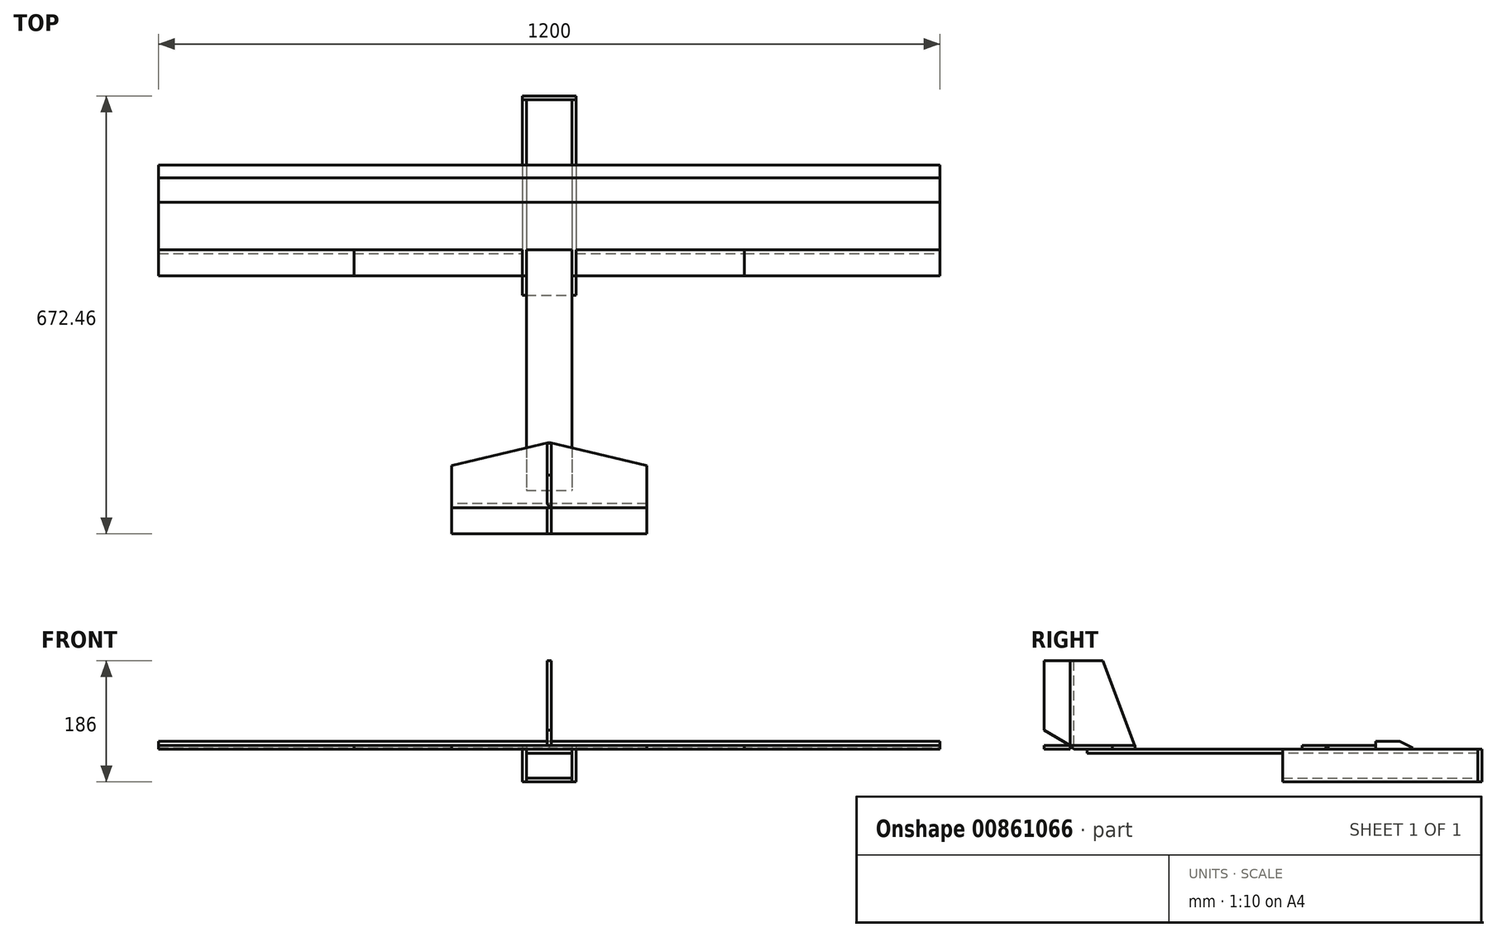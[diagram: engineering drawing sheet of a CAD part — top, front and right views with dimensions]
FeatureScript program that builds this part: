
annotation { "Feature Type Name" : "Feature", "Feature Type Description" : "" }
export const myFeature = defineFeature(function(context is Context, id is Id, definition is map)
    precondition{}
    {
        {
            var Q0;
            Q0=qCreatedBy(makeId("Top.planeOp"),FACE);
            var sketch = newSketch(context, id + "F0", { "sketchPlane" : qUnion([Q0])});
            skLineSegment(sketch, "E0.bottom", {"start": v(-35, 150) * mm, "end": v(35, 150) * mm});
            skLineSegment(sketch, "E0.top", {"start": v(-35, -150) * mm, "end": v(35, -150) * mm});
            skLineSegment(sketch, "E0.left", {"start": v(-35, 150) * mm, "end": v(-35, -150) * mm});
            skLineSegment(sketch, "E0.right", {"start": v(35, 150) * mm, "end": v(35, -150) * mm});
            skPoint(sketch, "E0.middle", {"position": v(0, 0) * mm});
            skLineSegment(sketch, "E1.top", {"start": v(-35, -450) * mm, "end": v(35, -450) * mm});
            skLineSegment(sketch, "E1.left", {"start": v(-35, -150) * mm, "end": v(-35, -450) * mm});
            skLineSegment(sketch, "E1.right", {"start": v(35, -150) * mm, "end": v(35, -450) * mm});
            skLineSegment(sketch, "E2.bottom", {"start": v(35, 150) * mm, "end": v(41, 150) * mm});
            skLineSegment(sketch, "E2.top", {"start": v(35, -150) * mm, "end": v(41, -150) * mm});
            skLineSegment(sketch, "E2.right", {"start": v(41, 150) * mm, "end": v(41, -150) * mm});
            skLineSegment(sketch, "E3.bottom", {"start": v(-35, 150) * mm, "end": v(-41, 150) * mm});
            skLineSegment(sketch, "E3.top", {"start": v(-35, -150) * mm, "end": v(-41, -150) * mm});
            skLineSegment(sketch, "E3.right", {"start": v(-41, 150) * mm, "end": v(-41, -150) * mm});
            skLineSegment(sketch, "E4.bottom", {"start": v(-41, -150) * mm, "end": v(-35, -150) * mm});
            skLineSegment(sketch, "E4.top", {"start": v(-41, -450) * mm, "end": v(-35, -450) * mm});
            skLineSegment(sketch, "E4.left", {"start": v(-41, -150) * mm, "end": v(-41, -450) * mm});
            skLineSegment(sketch, "E5.bottom", {"start": v(41, -150) * mm, "end": v(35, -150) * mm});
            skLineSegment(sketch, "E5.top", {"start": v(41, -450) * mm, "end": v(35, -450) * mm});
            skLineSegment(sketch, "E5.left", {"start": v(41, -150) * mm, "end": v(41, -450) * mm});
            skSolve(sketch);
        }
        {
            var Q0;
            Q0=makeQuery(id+"F0.imprint","IMPRINT",FACE,{"disambiguationData":[TD([[makeQuery(id+"F0.imprint","IMPRINT",EDGE,{"derivedFrom":sQuery(id+"F0.wireOp",EDGE,"E0.bottom")}),-1.0]])]});
            var Q1;
            Q1=makeQuery(id+"F0.imprint","IMPRINT",FACE,{"disambiguationData":[TD([[makeQuery(id+"F0.imprint","IMPRINT",EDGE,{"derivedFrom":sQuery(id+"F0.wireOp",EDGE,"E0.top")}),-1.0]])]});
            extrude(context, id + "F1", {"entities" : qUnion([Q0, Q1]), "oppositeDirection" : true, "depth" : 6 * mm, "offsetDistance" : 25 * mm});
        }
        {
            var Q0;
            Q0=makeQuery(id+"F0.imprint","IMPRINT",FACE,{"disambiguationData":[TD([[makeQuery(id+"F0.imprint","IMPRINT",EDGE,{"derivedFrom":sQuery(id+"F0.wireOp",EDGE,"E3.bottom")}),1.0]])]});
            var Q1;
            Q1=makeQuery(id+"F0.imprint","IMPRINT",FACE,{"disambiguationData":[TD([[makeQuery(id+"F0.imprint","IMPRINT",EDGE,{"derivedFrom":sQuery(id+"F0.wireOp",EDGE,"E2.bottom")}),-1.0]])]});
            var Q2;
            Q2=makeQuery(id+"F0.imprint","IMPRINT",FACE,{"disambiguationData":[TD([[makeQuery(id+"F0.imprint","IMPRINT",EDGE,{"derivedFrom":sQuery(id+"F0.wireOp",EDGE,"E5.bottom")}),1.0]])]});
            var Q3;
            Q3=makeQuery(id+"F0.imprint","IMPRINT",FACE,{"disambiguationData":[TD([[makeQuery(id+"F0.imprint","IMPRINT",EDGE,{"derivedFrom":sQuery(id+"F0.wireOp",EDGE,"E4.bottom")}),-1.0]])]});
            extrude(context, id + "F2", {"entities" : qUnion([Q0, Q1, Q2, Q3]), "oppositeDirection" : true, "depth" : 50 * mm, "offsetDistance" : 25 * mm});
        }
        {
            var Q0;
            Q0=makeQuery(id+"F2.opExtrude","SWEPT_FACE",FACE,{"disambiguationData":[OSD([sQuery(id+"F0.wireOp",EDGE,"E2.right"),sQuery(id+"F0.wireOp",EDGE,"E5.left")])]});
            var sketch = newSketch(context, id + "F3", { "sketchPlane" : qUnion([Q0])});
            skLineSegment(sketch, "E6", {"start": v(-150, 0) * mm, "end": v(-150, -50) * mm, "construction": true});
            skLineSegment(sketch, "E7", {"start": v(-150, -50) * mm, "end": v(-450, -15) * mm});
            skLineSegment(sketch, "E8", {"start": v(-450, -15) * mm, "end": v(-450, 0) * mm, "construction": true});
            skLineSegment(sketch, "E9", {"start": v(-450, 0) * mm, "end": v(-150, 0) * mm, "construction": true});
            skLineSegment(sketch, "E10", {"start": v(-450, -15) * mm, "end": v(-450, -50) * mm});
            skLineSegment(sketch, "E11", {"start": v(-450, -50) * mm, "end": v(-150, -50) * mm});
            skSolve(sketch);
        }
        {
            var Q0;
            Q0=makeQuery(id+"F2.opExtrude","SWEPT_FACE",FACE,{"disambiguationData":[OSD([sQuery(id+"F0.wireOp",EDGE,"E3.right"),sQuery(id+"F0.wireOp",EDGE,"E4.left")])]});
            var sketch = newSketch(context, id + "F4", { "sketchPlane" : qUnion([Q0])});
            skLineSegment(sketch, "E12", {"start": v(150, 0) * mm, "end": v(150, -50) * mm, "construction": true});
            skLineSegment(sketch, "E13", {"start": v(150, 0) * mm, "end": v(450, 0) * mm, "construction": true});
            skLineSegment(sketch, "E14", {"start": v(450, 0) * mm, "end": v(450, -15) * mm, "construction": true});
            skLineSegment(sketch, "E15", {"start": v(450, -15) * mm, "end": v(150, -50) * mm});
            skLineSegment(sketch, "E16", {"start": v(450, -50) * mm, "end": v(150, -50) * mm});
            skLineSegment(sketch, "E17", {"start": v(450, -15) * mm, "end": v(450, -50) * mm});
            skSolve(sketch);
        }
        {
            var Q0;
            Q0 = qSketchRegion(id + "F4", true);
            var Q1;
            Q1 = qSketchRegion(id + "F3", true);
            extrude(context, id + "F5", {"entities" : qUnion([Q0, Q1]), "operationType" : NewBodyOperationType.REMOVE, "endBound" : BoundingType.THROUGH_ALL, "depth" : 6 * mm, "offsetDistance" : 25 * mm});
        }
        {
            var Q0;
            Q0=makeQuery(id+"F2.opExtrude","SWEPT_FACE",FACE,{"disambiguationData":[OSD([sQuery(id+"F0.wireOp",EDGE,"E0.right"),sQuery(id+"F0.wireOp",EDGE,"E1.right")])]});
            var sketch = newSketch(context, id + "F6", { "sketchPlane" : qUnion([Q0])});
            skLineSegment(sketch, "E18.bottom", {"start": v(150, -50) * mm, "end": v(-150, -50) * mm});
            skLineSegment(sketch, "E18.top", {"start": v(150, -44) * mm, "end": v(-150, -44) * mm});
            skLineSegment(sketch, "E18.left", {"start": v(-150, -50) * mm, "end": v(-150, -44) * mm});
            skLineSegment(sketch, "E18.right", {"start": v(150, -50) * mm, "end": v(150, -44) * mm});
            skLineSegment(sketch, "E19", {"start": v(450, -15) * mm, "end": v(449.3, -9.04) * mm});
            skLineSegment(sketch, "E20", {"start": v(449.3, -9.04) * mm, "end": v(150, -44) * mm});
            skSolve(sketch);
        }
        {
            var Q0;
            Q0=makeQuery(id+"F6.imprint","IMPRINT",FACE,{"disambiguationData":[TD([[makeQuery(id+"F6.imprint","IMPRINT",EDGE,{"derivedFrom":sQuery(id+"F6.wireOp",EDGE,"E18.bottom")}),1.0]])]});
            var Q1;
            Q1=makeQuery(id+"F6.imprint","IMPRINT",FACE,{"disambiguationData":[TD([[makeQuery(id+"F6.imprint","IMPRINT",EDGE,{"derivedFrom":sQuery(id+"F6.wireOp",EDGE,"E18.right")}),-1.0]])]});
            extrude(context, id + "F7", {"entities" : qUnion([Q0, Q1]), "depth" : 70 * mm, "offsetDistance" : 25 * mm});
        }
        {
            var Q0;
            Q0=makeQuery(id+"F2.opExtrude","SWEPT_FACE",FACE,{"disambiguationData":[OSD([sQuery(id+"F0.wireOp",EDGE,"E2.bottom")])]});
            var sketch = newSketch(context, id + "F8", { "sketchPlane" : qUnion([Q0])});
            skLineSegment(sketch, "E21.bottom", {"start": v(-41, 0) * mm, "end": v(41, 0) * mm});
            skLineSegment(sketch, "E21.top", {"start": v(-41, -50) * mm, "end": v(41, -50) * mm});
            skLineSegment(sketch, "E21.left", {"start": v(-41, 0) * mm, "end": v(-41, -50) * mm});
            skLineSegment(sketch, "E21.right", {"start": v(41, 0) * mm, "end": v(41, -50) * mm});
            skPoint(sketch, "E21.middle", {"position": v(0, -25) * mm});
            skPoint(sketch, "E22.start.orphan", {"position": v(-35, -25) * mm});
            skSolve(sketch);
        }
        {
            var Q0;
            Q0 = qSketchRegion(id + "F8", true);
            extrude(context, id + "F9", {"entities" : qUnion([Q0]), "depth" : 6 * mm, "offsetDistance" : 25 * mm});
        }
        {
            var Q0;
            Q0=makeQuery(id+"F1.opExtrude","CAP_FACE",FACE,{"disambiguationData":[OSD([sQuery(id+"F0.wireOp",EDGE,"E0.bottom"),sQuery(id+"F0.wireOp",EDGE,"E1.top"),sQuery(id+"F0.wireOp",EDGE,"E0.right"),sQuery(id+"F0.wireOp",EDGE,"E0.left"),sQuery(id+"F0.wireOp",EDGE,"E1.left"),sQuery(id+"F0.wireOp",EDGE,"E1.right")])],"isStart":true});
            var sketch = newSketch(context, id + "F10", { "sketchPlane" : qUnion([Q0])});
            skLineSegment(sketch, "E23.bottom", {"start": v(150, -476.37) * mm, "end": v(-150, -476.37) * mm});
            skLineSegment(sketch, "E23.top", {"start": v(150, -376.37) * mm, "end": v(-150, -376.37) * mm});
            skLineSegment(sketch, "E23.left", {"start": v(150, -426.37) * mm, "end": v(150, -376.37) * mm});
            skLineSegment(sketch, "E23.right", {"start": v(-150, -426.37) * mm, "end": v(-150, -376.37) * mm});
            skPoint(sketch, "E23.middle", {"position": v(0, -426.37) * mm});
            skPoint(sketch, "E24", {"position": v(0, -450) * mm});
            skLineSegment(sketch, "E25", {"start": v(0, -426.37) * mm, "end": v(0, -376.37) * mm});
            skLineSegment(sketch, "E26", {"start": v(0, -426.37) * mm, "end": v(-150, -426.37) * mm, "construction": true});
            skLineSegment(sketch, "E27", {"start": v(0, -426.37) * mm, "end": v(150, -426.37) * mm, "construction": true});
            skLineSegment(sketch, "E28", {"start": v(0, -376.37) * mm, "end": v(-150, -411.37) * mm});
            skLineSegment(sketch, "E29", {"start": v(0, -376.37) * mm, "end": v(150, -411.37) * mm});
            skLineSegment(sketch, "E30", {"start": v(-150, -426.37) * mm, "end": v(-150, -476.37) * mm});
            skLineSegment(sketch, "E31", {"start": v(150, -476.37) * mm, "end": v(150, -426.37) * mm});
            skSolve(sketch);
        }
        {
            var Q0;
            Q0=makeQuery(id+"F10.imprint","IMPRINT",FACE,{"disambiguationData":[TD([[makeQuery(id+"F10.imprint","IMPRINT",EDGE,{"derivedFrom":sQuery(id+"F10.wireOp",EDGE,"E23.bottom")}),-1.0]])]});
            var Q1;
            {var subQ1=makeQuery(id+"F1.opExtrude","CAP_EDGE",EDGE,{"disambiguationData":[OSD([sQuery(id+"F0.wireOp",EDGE,"E1.top")])],"isStart":true});Q1=makeQuery(id+"F10.imprint","IMPRINT",FACE,{"disambiguationData":[TD([[makeQuery(id+"F10.imprint","IMPRINT",EDGE,{"derivedFrom":subQ1}),1.0]])]});}
            extrude(context, id + "F11", {"entities" : qUnion([Q0, Q1]), "depth" : 6 * mm, "offsetDistance" : 25 * mm});
        }
        {
            var Q0;
            Q0=makeQuery(id+"F1.opExtrude","CAP_FACE",FACE,{"disambiguationData":[OSD([sQuery(id+"F0.wireOp",EDGE,"E0.bottom"),sQuery(id+"F0.wireOp",EDGE,"E1.top"),sQuery(id+"F0.wireOp",EDGE,"E0.right"),sQuery(id+"F0.wireOp",EDGE,"E0.left"),sQuery(id+"F0.wireOp",EDGE,"E1.left"),sQuery(id+"F0.wireOp",EDGE,"E1.right")])],"isStart":true});
            var sketch = newSketch(context, id + "F12", { "sketchPlane" : qUnion([Q0])});
            skLineSegment(sketch, "E32", {"start": v(0, 60) * mm, "end": v(0, -90) * mm, "construction": true});
            skLineSegment(sketch, "E33.bottom", {"start": v(-600, 50) * mm, "end": v(600, 50) * mm});
            skLineSegment(sketch, "E33.top", {"start": v(-600, -80) * mm, "end": v(600, -80) * mm});
            skLineSegment(sketch, "E33.left", {"start": v(-600, 50) * mm, "end": v(-600, -80) * mm});
            skLineSegment(sketch, "E33.right", {"start": v(600, 50) * mm, "end": v(600, -80) * mm});
            skPoint(sketch, "E33.middle", {"position": v(0, -15) * mm});
            skLineSegment(sketch, "E34", {"start": v(-600, -7.2) * mm, "end": v(600, -7.2) * mm});
            skLineSegment(sketch, "E35.bottom", {"start": v(-41, -80) * mm, "end": v(41, -80) * mm});
            skLineSegment(sketch, "E35.top", {"start": v(-41, -120) * mm, "end": v(41, -120) * mm});
            skLineSegment(sketch, "E35.left", {"start": v(-41, -80) * mm, "end": v(-41, -120) * mm});
            skLineSegment(sketch, "E35.right", {"start": v(41, -80) * mm, "end": v(41, -120) * mm});
            skSolve(sketch);
        }
        {
            var Q0;
            {var subQ0=sQuery(id+"F12.wireOp",EDGE,"E33.left");var subQ1=sQuery(id+"F12.wireOp",EDGE,"E33.top");var subQ2=makeQuery(id+"F12.imprint","INTERSECT",VERTEX,{"derivedFrom":[subQ1,subQ0]});Q0=makeQuery(id+"F12.imprint","IMPRINT",FACE,{"disambiguationData":[TD([[makeQuery(id+"F12.imprint","IMPRINT",EDGE,{"disambiguationData":[TD([[subQ2,1.0]])],"derivedFrom":subQ0}),1.0]])]});}
            var Q1;
            {var subQ0=sQuery(id+"F12.wireOp",EDGE,"E33.right");var subQ1=sQuery(id+"F12.wireOp",EDGE,"E33.top");var subQ2=makeQuery(id+"F12.imprint","INTERSECT",VERTEX,{"derivedFrom":[subQ1,subQ0]});Q1=makeQuery(id+"F12.imprint","IMPRINT",FACE,{"disambiguationData":[TD([[makeQuery(id+"F12.imprint","IMPRINT",EDGE,{"disambiguationData":[TD([[subQ2,1.0]])],"derivedFrom":subQ0}),-1.0]])]});}
            var Q2;
            {var subQ0=sQuery(id+"F12.wireOp",EDGE,"E33.top");var subQ1=makeQuery(id+"F1.opExtrude","CAP_EDGE",EDGE,{"disambiguationData":[OSD([sQuery(id+"F0.wireOp",EDGE,"E0.left"),sQuery(id+"F0.wireOp",EDGE,"E1.left")])],"isStart":true});var subQ2=makeQuery(id+"F12.imprint","INTERSECT",VERTEX,{"derivedFrom":[subQ1,subQ0]});Q2=makeQuery(id+"F12.imprint","IMPRINT",FACE,{"disambiguationData":[TD([[makeQuery(id+"F12.imprint","IMPRINT",EDGE,{"disambiguationData":[TD([[subQ2,-1.0]])],"derivedFrom":subQ0}),1.0]])]});}
            var Q3;
            {var subQ0=sQuery(id+"F12.wireOp",EDGE,"E34");var subQ1=makeQuery(id+"F1.opExtrude","CAP_EDGE",EDGE,{"disambiguationData":[OSD([sQuery(id+"F0.wireOp",EDGE,"E0.left"),sQuery(id+"F0.wireOp",EDGE,"E1.left")])],"isStart":true});var subQ2=makeQuery(id+"F12.imprint","INTERSECT",VERTEX,{"derivedFrom":[subQ1,subQ0]});Q3=makeQuery(id+"F12.imprint","IMPRINT",FACE,{"disambiguationData":[TD([[makeQuery(id+"F12.imprint","IMPRINT",EDGE,{"disambiguationData":[TD([[subQ2,-1.0]])],"derivedFrom":subQ0}),-1.0]])]});}
            var Q4;
            {var subQ0=sQuery(id+"F12.wireOp",EDGE,"E35.bottom");var subQ1=makeQuery(id+"F1.opExtrude","CAP_EDGE",EDGE,{"disambiguationData":[OSD([sQuery(id+"F0.wireOp",EDGE,"E0.left"),sQuery(id+"F0.wireOp",EDGE,"E1.left")])],"isStart":true});var subQ2=makeQuery(id+"F12.imprint","INTERSECT",VERTEX,{"derivedFrom":[subQ1,subQ0]});Q4=makeQuery(id+"F12.imprint","IMPRINT",FACE,{"disambiguationData":[TD([[makeQuery(id+"F12.imprint","IMPRINT",EDGE,{"disambiguationData":[TD([[subQ2,-1.0]])],"derivedFrom":subQ0}),-1.0]])]});}
            var Q5;
            {var subQ0=sQuery(id+"F12.wireOp",EDGE,"E35.right");Q5=makeQuery(id+"F12.imprint","IMPRINT",FACE,{"disambiguationData":[TD([[makeQuery(id+"F12.imprint","IMPRINT",EDGE,{"derivedFrom":subQ0}),-1.0]])]});}
            var Q6;
            {var subQ0=sQuery(id+"F12.wireOp",EDGE,"E35.left");Q6=makeQuery(id+"F12.imprint","IMPRINT",FACE,{"disambiguationData":[TD([[makeQuery(id+"F12.imprint","IMPRINT",EDGE,{"derivedFrom":subQ0}),1.0]])]});}
            extrude(context, id + "F13", {"entities" : qUnion([Q0, Q1, Q2, Q3, Q4, Q5, Q6]), "depth" : 6 * mm, "offsetDistance" : 25 * mm});
        }
        {
            var Q0;
            {var subQ0=sQuery(id+"F12.wireOp",EDGE,"f9qtTOJY-V2A6-egXc-k2BP-GJsxi0lqYclH");var subQ1=sQuery(id+"F12.wireOp",EDGE,"LZZIuyLF-FcuM-KAbS-gqD7-LItA6hUNZmsj");var subQ2=makeQuery(id+"F12.imprint","INTERSECT",VERTEX,{"derivedFrom":[subQ1,subQ0]});Q0=makeQuery(id+"F12.imprint","IMPRINT",FACE,{"disambiguationData":[TD([[makeQuery(id+"F12.imprint","IMPRINT",EDGE,{"disambiguationData":[TD([[subQ2,-1.0]])],"derivedFrom":subQ0}),1.0]])]});}
            var Q1;
            {var subQ5=sQuery(id+"F12.wireOp",EDGE,"1fCqvdx0-kBV5-oBVe-sgTc-qIVpe4zWd1In");var subQ7=sQuery(id+"F12.wireOp",EDGE,"LZZIuyLF-FcuM-KAbS-gqD7-LItA6hUNZmsj");var subQ8=makeQuery(id+"F12.imprint","INTERSECT",VERTEX,{"derivedFrom":[subQ7,subQ5]});Q1=makeQuery(id+"F12.imprint","IMPRINT",FACE,{"disambiguationData":[TD([[makeQuery(id+"F12.imprint","IMPRINT",EDGE,{"disambiguationData":[TD([[subQ8,-1.0]])],"derivedFrom":subQ7}),1.0]])]});}
            var Q2;
            {var subQ0=sQuery(id+"F12.wireOp",EDGE,"7Yiizx21-BXyQ-pYym-OMHb-G3uuBtVVquUZ");var subQ1=sQuery(id+"F12.wireOp",EDGE,"1fCqvdx0-kBV5-oBVe-sgTc-qIVpe4zWd1In");var subQ2=makeQuery(id+"F12.imprint","INTERSECT",VERTEX,{"derivedFrom":[subQ1,subQ0]});Q2=makeQuery(id+"F12.imprint","IMPRINT",FACE,{"disambiguationData":[TD([[makeQuery(id+"F12.imprint","IMPRINT",EDGE,{"disambiguationData":[TD([[subQ2,-1.0]])],"derivedFrom":subQ0}),-1.0]])]});}
            var Q3;
            {var subQ0=sQuery(id+"F12.wireOp",EDGE,"E33.left");var subQ1=sQuery(id+"F12.wireOp",EDGE,"E33.bottom");var subQ2=makeQuery(id+"F12.imprint","INTERSECT",VERTEX,{"derivedFrom":[subQ1,subQ0]});Q3=makeQuery(id+"F12.imprint","IMPRINT",FACE,{"disambiguationData":[TD([[makeQuery(id+"F12.imprint","IMPRINT",EDGE,{"disambiguationData":[TD([[subQ2,-1.0]])],"derivedFrom":subQ0}),1.0]])]});}
            var Q4;
            {var subQ0=sQuery(id+"F12.wireOp",EDGE,"E33.right");var subQ1=sQuery(id+"F12.wireOp",EDGE,"E33.bottom");var subQ2=makeQuery(id+"F12.imprint","INTERSECT",VERTEX,{"derivedFrom":[subQ1,subQ0]});Q4=makeQuery(id+"F12.imprint","IMPRINT",FACE,{"disambiguationData":[TD([[makeQuery(id+"F12.imprint","IMPRINT",EDGE,{"disambiguationData":[TD([[subQ2,-1.0]])],"derivedFrom":subQ0}),-1.0]])]});}
            var Q5;
            {var subQ0=sQuery(id+"F12.wireOp",EDGE,"E33.bottom");var subQ1=makeQuery(id+"F1.opExtrude","CAP_EDGE",EDGE,{"disambiguationData":[OSD([sQuery(id+"F0.wireOp",EDGE,"E0.left"),sQuery(id+"F0.wireOp",EDGE,"E1.left")])],"isStart":true});var subQ2=makeQuery(id+"F12.imprint","INTERSECT",VERTEX,{"derivedFrom":[subQ1,subQ0]});Q5=makeQuery(id+"F12.imprint","IMPRINT",FACE,{"disambiguationData":[TD([[makeQuery(id+"F12.imprint","IMPRINT",EDGE,{"disambiguationData":[TD([[subQ2,-1.0]])],"derivedFrom":subQ0}),-1.0]])]});}
            extrude(context, id + "F14", {"entities" : qUnion([Q0, Q1, Q2, Q3, Q4, Q5]), "depth" : 12 * mm, "offsetDistance" : 25 * mm});
        }
        {
            var Q0;
            Q0=makeQuery(id+"F14.opExtrude","CAP_EDGE",EDGE,{"disambiguationData":[OSD([sQuery(id+"F12.wireOp",EDGE,"E33.bottom")])],"isStart":false});
            chamfer(context, id + "F15", {"entities" : qUnion([Q0]), "chamferType" : ChamferType.TWO_OFFSETS, "width1" : 10 * mm, "oppositeDirection" : false, "width2" : 20 * mm, "tangentPropagation" : true});
        }
        {
            var Q0;
            Q0=makeQuery(id+"F11.opExtrude","CAP_FACE",FACE,{"disambiguationData":[OSD([sQuery(id+"F10.wireOp",EDGE,"E23.bottom"),sQuery(id+"F10.wireOp",EDGE,"E23.left"),sQuery(id+"F10.wireOp",EDGE,"E23.right"),sQuery(id+"F10.wireOp",EDGE,"E28"),sQuery(id+"F10.wireOp",EDGE,"E29"),sQuery(id+"F10.wireOp",EDGE,"E30"),sQuery(id+"F10.wireOp",EDGE,"E31")])],"isStart":false});
            var Q1;
            Q1=sQuery(id+"F10.wireOp",EDGE,"E25");
            cPlane(context, id + "F16", {"entities" : qUnion([Q0, Q1]), "cplaneType" : CPlaneType.LINE_ANGLE, "offset" : 25 * mm, "angle" : 90 * degree, "width" : 150 * mm, "height" : 150 * mm});
        }
        {
            var Q0;
            Q0=qCreatedBy(id+"F16.planeOp",FACE);
            var sketch = newSketch(context, id + "F17", { "sketchPlane" : qUnion([Q0])});
            skLineSegment(sketch, "E36", {"start": v(476.46, 6) * mm, "end": v(476.46, 136) * mm});
            skLineSegment(sketch, "E37", {"start": v(476.46, 136) * mm, "end": v(426.46, 136) * mm});
            skLineSegment(sketch, "E38", {"start": v(426.46, 136) * mm, "end": v(377.29, 6) * mm});
            skLineSegment(sketch, "E39", {"start": v(377.29, 6) * mm, "end": v(476.46, 6) * mm});
            skSolve(sketch);
        }
        {
            var Q0;
            Q0=makeQuery(id+"F17.imprint","IMPRINT",FACE,{"disambiguationData":[TD([[makeQuery(id+"F17.imprint","IMPRINT",EDGE,{"derivedFrom":sQuery(id+"F17.wireOp",EDGE,"E36")}),1.0]])]});
            extrude(context, id + "F18", {"entities" : qUnion([Q0]), "depth" : 6 * mm, "offsetDistance" : 25 * mm, "symmetric" : true});
        }
        {
            var Q0;
            Q0=makeQuery(id+"F11.opExtrude","CAP_FACE",FACE,{"disambiguationData":[OSD([sQuery(id+"F10.wireOp",EDGE,"E23.bottom"),sQuery(id+"F10.wireOp",EDGE,"E23.left"),sQuery(id+"F10.wireOp",EDGE,"E23.right"),sQuery(id+"F10.wireOp",EDGE,"E28"),sQuery(id+"F10.wireOp",EDGE,"E29"),sQuery(id+"F10.wireOp",EDGE,"E30"),sQuery(id+"F10.wireOp",EDGE,"E31")])],"isStart":false});
            var sketch = newSketch(context, id + "F19", { "sketchPlane" : qUnion([Q0])});
            skLineSegment(sketch, "E40.bottom", {"start": v(-150, -476.37) * mm, "end": v(150, -476.37) * mm});
            skLineSegment(sketch, "E40.top", {"start": v(-150, -516.37) * mm, "end": v(150, -516.37) * mm});
            skLineSegment(sketch, "E40.left", {"start": v(-150, -476.37) * mm, "end": v(-150, -516.37) * mm});
            skLineSegment(sketch, "E40.right", {"start": v(150, -476.37) * mm, "end": v(150, -516.37) * mm});
            skSolve(sketch);
        }
        {
            var Q0;
            Q0=makeQuery(id+"F19.imprint","IMPRINT",FACE,{"disambiguationData":[TD([[makeQuery(id+"F19.imprint","IMPRINT",EDGE,{"derivedFrom":sQuery(id+"F19.wireOp",EDGE,"E40.bottom")}),1.0]])]});
            extrude(context, id + "F20", {"entities" : qUnion([Q0]), "oppositeDirection" : true, "depth" : 6 * mm, "offsetDistance" : 25 * mm});
        }
        {
            var Q0;
            Q0=makeQuery(id+"F11.opExtrude","CAP_EDGE",EDGE,{"disambiguationData":[OSD([sQuery(id+"F10.wireOp",EDGE,"E23.bottom")])],"isStart":true});
            chamfer(context, id + "F21", {"entities" : qUnion([Q0]), "width" : 6 * mm, "tangentPropagation" : true});
        }
        {
            var Q0;
            Q0=makeQuery(id+"F18.opExtrude","CAP_FACE",FACE,{"disambiguationData":[OSD([sQuery(id+"F17.wireOp",EDGE,"E36"),sQuery(id+"F17.wireOp",EDGE,"E37"),sQuery(id+"F17.wireOp",EDGE,"E38"),sQuery(id+"F17.wireOp",EDGE,"E39")])],"isStart":true});
            var sketch = newSketch(context, id + "F22", { "sketchPlane" : qUnion([Q0])});
            skLineSegment(sketch, "E41.bottom", {"start": v(-476.46, 136) * mm, "end": v(-516.46, 136) * mm});
            skLineSegment(sketch, "E41.top", {"start": v(-476.46, 6) * mm, "end": v(-516.46, 6) * mm});
            skLineSegment(sketch, "E41.left", {"start": v(-476.46, 136) * mm, "end": v(-476.46, 6) * mm});
            skLineSegment(sketch, "E41.right", {"start": v(-516.46, 136) * mm, "end": v(-516.46, 29.1) * mm});
            skLineSegment(sketch, "E42", {"start": v(-476.46, 6) * mm, "end": v(-516.46, 29.1) * mm});
            skSolve(sketch);
        }
        {
            var Q0;
            Q0=makeQuery(id+"F22.imprint","IMPRINT",FACE,{"disambiguationData":[TD([[makeQuery(id+"F22.imprint","IMPRINT",EDGE,{"derivedFrom":sQuery(id+"F22.wireOp",EDGE,"E41.bottom")}),1.0]])]});
            extrude(context, id + "F23", {"entities" : qUnion([Q0]), "oppositeDirection" : true, "depth" : 6 * mm, "offsetDistance" : 25 * mm});
        }
        {
            var Q0;
            Q0=makeQuery(id+"F18.opExtrude","CAP_EDGE",EDGE,{"disambiguationData":[OSD([sQuery(id+"F17.wireOp",EDGE,"E36")])],"isStart":false});
            chamfer(context, id + "F24", {"entities" : qUnion([Q0]), "width" : 6 * mm, "tangentPropagation" : true});
        }
        {
            var Q0;
            Q0=makeQuery(id+"F13.opExtrude","CAP_FACE",FACE,{"disambiguationData":[OSD([sQuery(id+"F12.wireOp",EDGE,"E33.top"),sQuery(id+"F12.wireOp",EDGE,"E33.left"),sQuery(id+"F12.wireOp",EDGE,"E33.right"),sQuery(id+"F12.wireOp",EDGE,"E34")])],"isStart":false});
            var sketch = newSketch(context, id + "F25", { "sketchPlane" : qUnion([Q0])});
            skLineSegment(sketch, "E43.bottom", {"start": v(-600, -80) * mm, "end": v(-300, -80) * mm});
            skLineSegment(sketch, "E43.top", {"start": v(-600, -120) * mm, "end": v(-300, -120) * mm});
            skLineSegment(sketch, "E43.left", {"start": v(-600, -80) * mm, "end": v(-600, -120) * mm});
            skLineSegment(sketch, "E43.right", {"start": v(-300, -80) * mm, "end": v(-300, -120) * mm});
            skLineSegment(sketch, "E44.bottom", {"start": v(600, -80) * mm, "end": v(300, -80) * mm});
            skLineSegment(sketch, "E44.top", {"start": v(600, -120) * mm, "end": v(300, -120) * mm});
            skLineSegment(sketch, "E44.left", {"start": v(600, -80) * mm, "end": v(600, -120) * mm});
            skLineSegment(sketch, "E44.right", {"start": v(300, -80) * mm, "end": v(300, -120) * mm});
            skLineSegment(sketch, "E45.bottom", {"start": v(-300, -80) * mm, "end": v(-41, -80) * mm});
            skLineSegment(sketch, "E45.top", {"start": v(-300, -120) * mm, "end": v(-41, -120) * mm});
            skLineSegment(sketch, "E45.right", {"start": v(-41, -80) * mm, "end": v(-41, -120) * mm});
            skLineSegment(sketch, "E46.bottom", {"start": v(41, -80) * mm, "end": v(300, -80) * mm});
            skLineSegment(sketch, "E46.top", {"start": v(41, -120) * mm, "end": v(300, -120) * mm});
            skLineSegment(sketch, "E46.left", {"start": v(41, -80) * mm, "end": v(41, -120) * mm});
            skSolve(sketch);
        }
        {
            var Q0;
            Q0=makeQuery(id+"F25.imprint","IMPRINT",FACE,{"disambiguationData":[TD([[makeQuery(id+"F25.imprint","IMPRINT",EDGE,{"derivedFrom":sQuery(id+"F25.wireOp",EDGE,"E43.bottom")}),-1.0]])]});
            var Q1;
            Q1=makeQuery(id+"F25.imprint","IMPRINT",FACE,{"disambiguationData":[TD([[makeQuery(id+"F25.imprint","IMPRINT",EDGE,{"derivedFrom":sQuery(id+"F25.wireOp",EDGE,"E44.bottom")}),-1.0]])]});
            extrude(context, id + "F26", {"entities" : qUnion([Q0, Q1]), "oppositeDirection" : true, "depth" : 6 * mm, "offsetDistance" : 25 * mm});
        }
        {
            var Q0;
            Q0=makeQuery(id+"F25.imprint","IMPRINT",FACE,{"disambiguationData":[TD([[makeQuery(id+"F25.imprint","IMPRINT",EDGE,{"derivedFrom":sQuery(id+"F25.wireOp",EDGE,"E45.bottom")}),-1.0]])]});
            var Q1;
            Q1=makeQuery(id+"F25.imprint","IMPRINT",FACE,{"disambiguationData":[TD([[makeQuery(id+"F25.imprint","IMPRINT",EDGE,{"derivedFrom":sQuery(id+"F25.wireOp",EDGE,"E46.bottom")}),-1.0]])]});
            extrude(context, id + "F27", {"entities" : qUnion([Q0, Q1]), "oppositeDirection" : true, "depth" : 6 * mm, "offsetDistance" : 25 * mm});
        }
        {
            var Q0;
            Q0=makeQuery(id+"F26.opExtrude","CAP_EDGE",EDGE,{"disambiguationData":[OSD([sQuery(id+"F25.wireOp",EDGE,"E43.bottom")])],"isStart":false});
            var Q1;
            Q1=makeQuery(id+"F26.opExtrude","CAP_EDGE",EDGE,{"disambiguationData":[OSD([sQuery(id+"F25.wireOp",EDGE,"E44.bottom")])],"isStart":false});
            var Q2;
            Q2=makeQuery(id+"F27.opExtrude","CAP_EDGE",EDGE,{"disambiguationData":[OSD([sQuery(id+"F25.wireOp",EDGE,"E45.bottom")])],"isStart":false});
            var Q3;
            Q3=makeQuery(id+"F27.opExtrude","CAP_EDGE",EDGE,{"disambiguationData":[OSD([sQuery(id+"F25.wireOp",EDGE,"E46.bottom")])],"isStart":false});
            chamfer(context, id + "F28", {"entities" : qUnion([Q0, Q1, Q2, Q3]), "width" : 6 * mm, "tangentPropagation" : true});
        }
    });
